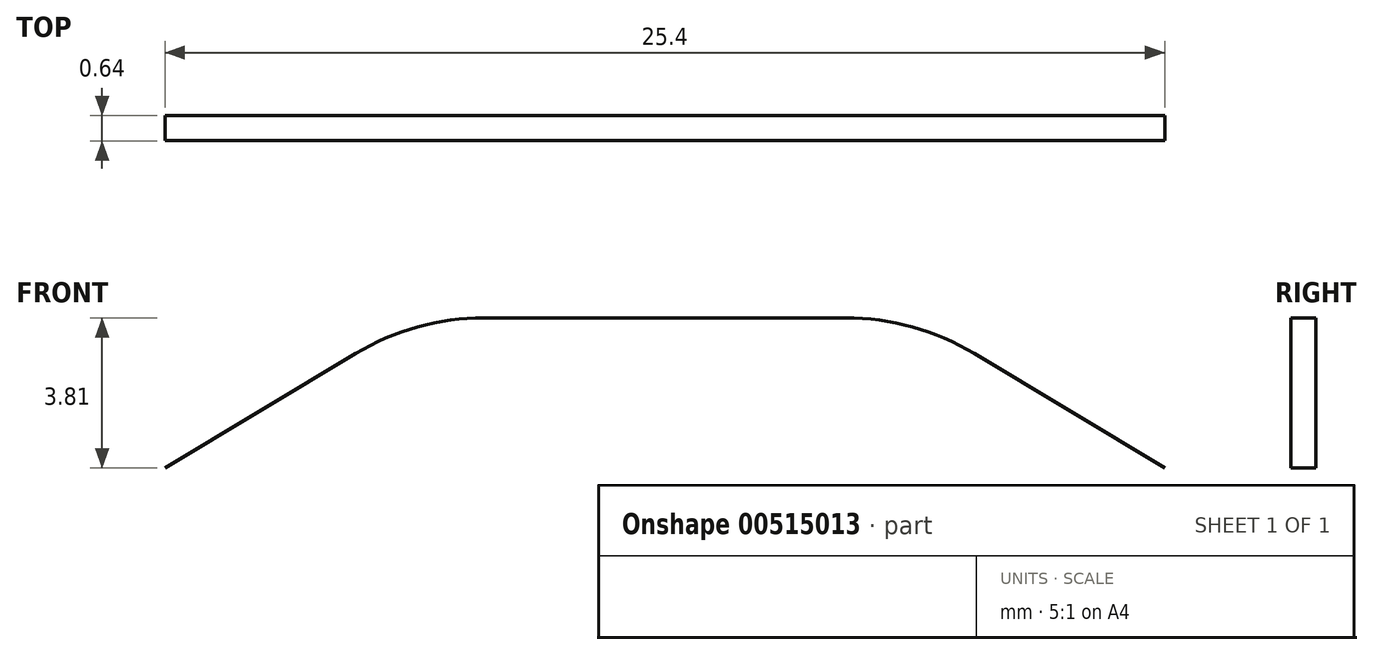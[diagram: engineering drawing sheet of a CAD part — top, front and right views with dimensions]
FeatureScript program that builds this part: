
annotation { "Feature Type Name" : "Feature", "Feature Type Description" : "" }
export const myFeature = defineFeature(function(context is Context, id is Id, definition is map)
    precondition{}
    {
        {
            var Q0;
            Q0=qCreatedBy(makeId("Front.planeOp"),FACE);
            var sketch = newSketch(context, id + "F0", { "sketchPlane" : qUnion([Q0])});
            skPoint(sketch, "E0.center.orphan", {"position": v(0, 3.8) * mm});
            skPoint(sketch, "E0.end.orphan", {"position": v(-12.7, 0) * mm});
            skPoint(sketch, "E0.start.orphan", {"position": v(12.7, 0) * mm});
            skPoint(sketch, "E1", {"position": v(-6.35, 3.8) * mm});
            skPoint(sketch, "E2", {"position": v(6.35, 3.81) * mm});
            skLineSegment(sketch, "E3", {"start": v(-4.6, 3.8) * mm, "end": v(4.6, 3.81) * mm});
            skLineSegment(sketch, "E4", {"start": v(-12.7, 0) * mm, "end": v(-7.86, 2.9) * mm});
            skLineSegment(sketch, "E5", {"start": v(7.86, 2.9) * mm, "end": v(12.7, 0) * mm});
            skArc(sketch, "E6.filletArc", {"start": v(-4.6, 3.8) * mm, "mid": v(-6.29, 3.58) * mm, "end": v(-7.86, 2.9) * mm});
            skArc(sketch, "E7.filletArc", {"start": v(7.86, 2.9) * mm, "mid": v(6.29, 3.58) * mm, "end": v(4.6, 3.8) * mm});
            skSolve(sketch);
        }
        {
            var Q0;
            Q0 = qSketchRegion(id + "F0", true);
            var Q1;
            Q1=sQuery(id+"F0.wireOp",EDGE,"E3");
            var Q2;
            Q2=sQuery(id+"F0.wireOp",EDGE,"E6.filletArc");
            var Q3;
            Q3=sQuery(id+"F0.wireOp",EDGE,"E4");
            var Q4;
            Q4=sQuery(id+"F0.wireOp",EDGE,"E7.filletArc");
            var Q5;
            Q5=sQuery(id+"F0.wireOp",EDGE,"E5");
            extrude(context, id + "F1", {"entities" : qUnion([Q0]), "bodyType" : ToolBodyType.SURFACE, "surfaceEntities" : qUnion([Q1, Q2, Q3, Q4, Q5]), "depth" : 0.64 * mm, "offsetDistance" : 25.4 * mm});
        }
    });
